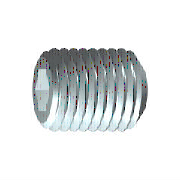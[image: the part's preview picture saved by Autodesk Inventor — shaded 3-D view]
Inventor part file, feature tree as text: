
AUTODESK INVENTOR PART (.ipt)
format: ipt  version: 2018 (Build 220112000, 112)  size: 163,328 bytes
history: native  units: mm (DEFAULTED — no unit token found)
features: sketch x2, extrude x1, other x1, plane x1
ambient origin geometry x8: Origin, YZ Plane, XZ Plane, XY Plane, X Axis, Y Axis, Z Axis, Center Point
bodies: Solid1 (feature_tree), Body (feature_tree)
feature tree (5):
  extrude  "Slot"  TaperAngle=60.0deg  [1 undecoded]
  other  "Work Axis1"
  plane  "Work Plane1"
  sketch  "Sketch1"  dims[d0=2.1mm d1=60.0deg]
  sketch  "Sketch2"  dims[d2=3.0mm d3=1.732051mm d6=90.0deg d4=0.0mm d5=5.0mm d7=0.306725mm d8=45.0deg d21=10.0mm d9=0.0mm d11=5.0mm d12=0.0mm d13=0.306725mm d14=45.0deg d15=0.0mm d29=0.306725mm d30=0.306725mm d31=0.0mm]
note: 1 required parameter value undecoded (feature->parameter linkage not recoverable at this tier; creation-order binding heuristic only, values carry confidence <= 0.55)
